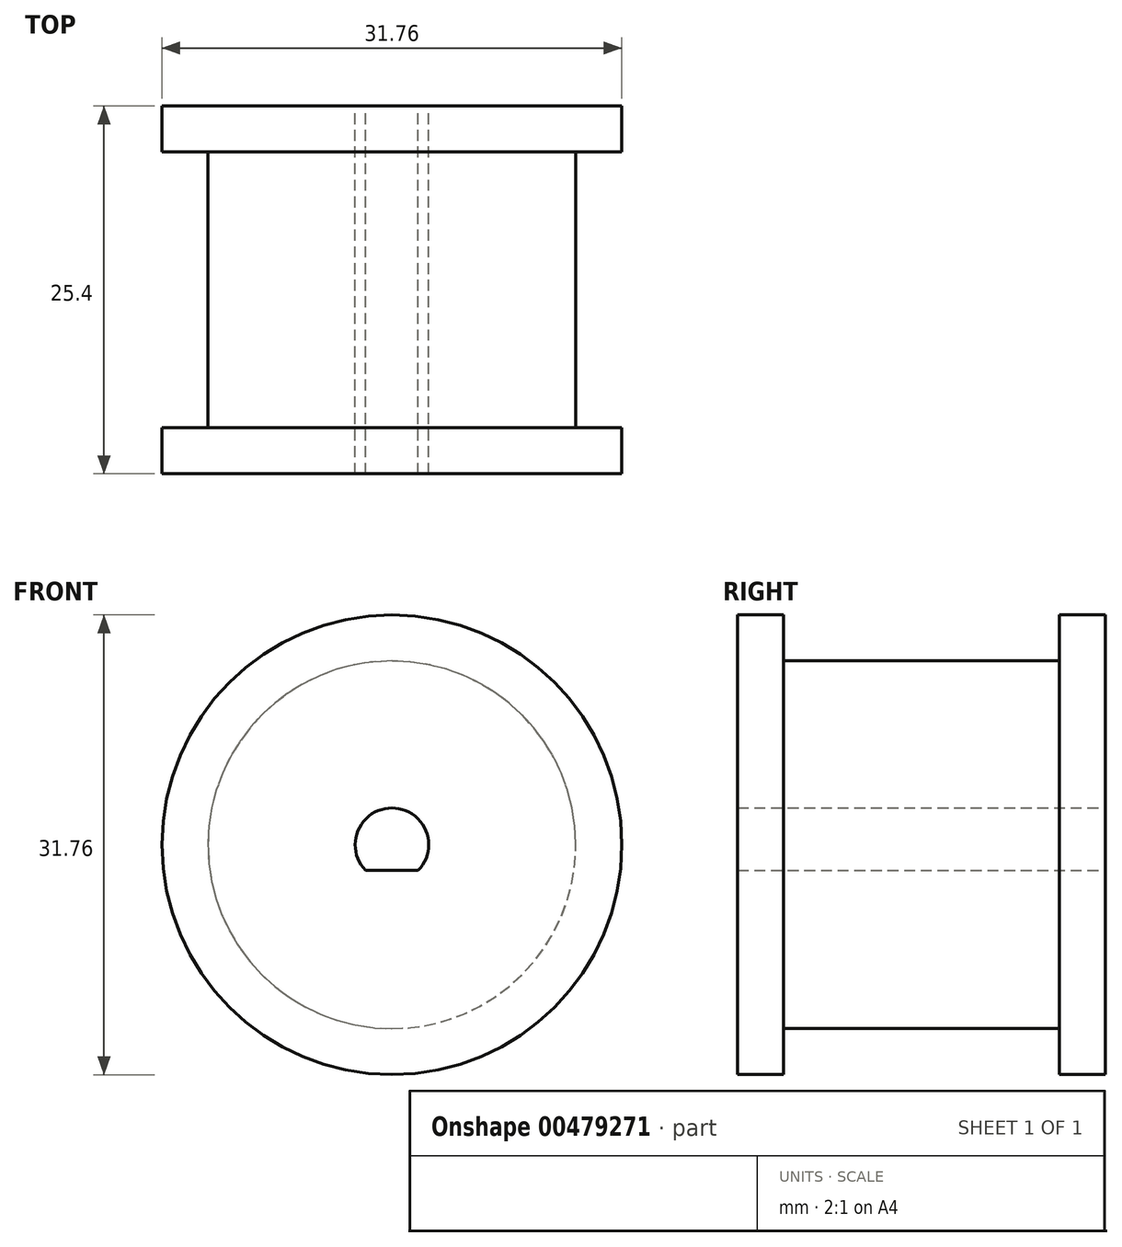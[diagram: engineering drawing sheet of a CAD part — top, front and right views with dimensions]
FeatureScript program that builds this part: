
annotation { "Feature Type Name" : "Feature", "Feature Type Description" : "" }
export const myFeature = defineFeature(function(context is Context, id is Id, definition is map)
    precondition{}
    {
        {
            var Q0;
            Q0=qCreatedBy(makeId("Front.planeOp"),FACE);
            var sketch = newSketch(context, id + "F0", { "sketchPlane" : qUnion([Q0])});
            skCircle(sketch, "E0", {"center": v(0, 0) * mm, "radius": 2.54 * mm});
            skLineSegment(sketch, "E1", {"start": v(-1.81, -1.78) * mm, "end": v(1.81, -1.78) * mm});
            skCircle(sketch, "E2", {"center": v(0, 0) * mm, "radius": 12.7 * mm});
            skSolve(sketch);
        }
        {
            var Q0;
            Q0 = qSketchRegion(id + "F0", true);
            var Q1;
            {var subQ0=sQuery(id+"F0.wireOp",EDGE,"E1");Q1=makeQuery(id+"F0.imprint","IMPRINT",FACE,{"disambiguationData":[TD([[makeQuery(id+"F0.imprint","IMPRINT",EDGE,{"derivedFrom":subQ0}),-1.0]])]});}
            extrude(context, id + "F1", {"entities" : qUnion([Q0, Q1]), "depth" : 25.4 * mm});
        }
        {
            var Q0;
            Q0=makeQuery(id+"F1.opExtrude","CAP_FACE",FACE,{"disambiguationData":[OSD([sQuery(id+"F0.wireOp",EDGE,"E0"),sQuery(id+"F0.wireOp",EDGE,"E2")])],"isStart":false});
            var sketch = newSketch(context, id + "F2", { "sketchPlane" : qUnion([Q0])});
            skCircle(sketch, "E3", {"center": v(0, 0) * mm, "radius": 15.88 * mm});
            skSolve(sketch);
        }
        {
            var Q0;
            Q0=makeQuery(id+"F2.imprint","IMPRINT",FACE,{"disambiguationData":[TD([[makeQuery(id+"F2.imprint","IMPRINT",EDGE,{"derivedFrom":sQuery(id+"F2.wireOp",EDGE,"E3")}),1.0]])]});
            var Q1;
            Q1=makeQuery(id+"F2.imprint","IMPRINT",FACE,{"disambiguationData":[TD([[makeQuery(id+"F2.imprint","IMPRINT",EDGE,{"derivedFrom":makeQuery(id+"F1.opExtrude","CAP_EDGE",EDGE,{"disambiguationData":[OSD([sQuery(id+"F0.wireOp",EDGE,"E0")])],"isStart":false})}),-1.0]])]});
            extrude(context, id + "F3", {"entities" : qUnion([Q0, Q1]), "operationType" : NewBodyOperationType.ADD, "oppositeDirection" : true, "depth" : 3.17 * mm});
        }
        {
            var Q0;
            Q0=makeQuery(id+"F1.opExtrude","CAP_FACE",FACE,{"disambiguationData":[OSD([sQuery(id+"F0.wireOp",EDGE,"E0"),sQuery(id+"F0.wireOp",EDGE,"E1"),sQuery(id+"F0.wireOp",EDGE,"E2")])],"isStart":true});
            var Q1;
            {var subQ0=sQuery(id+"F0.wireOp",EDGE,"E1");var subQ1=sQuery(id+"F0.wireOp",EDGE,"E0");Q1=makeQuery(id+"F3.boolean.opBoolean","MERGE",FACE,{"derivedFrom":[makeQuery(id+"F1.opExtrude","CAP_FACE",FACE,{"disambiguationData":[OSD([subQ1,subQ0,sQuery(id+"F0.wireOp",EDGE,"E2")])],"isStart":false}),makeQuery(id+"F3.opExtrude","CAP_FACE",FACE,{"disambiguationData":[OSD([subQ1,subQ0,sQuery(id+"F2.wireOp",EDGE,"E3")])],"isStart":true})]});}
            cPlane(context, id + "F4", {"entities" : qUnion([Q0, Q1]), "cplaneType" : CPlaneType.MID_PLANE, "offset" : 25.4 * mm, "width" : 152.4 * mm, "height" : 152.4 * mm});
        }
        {
            var Q0;
            Q0=makeQuery(id+"F1.opExtrude","SWEPT_BODY",BODY,{"disambiguationData":[OSD([sQuery(id+"F0.wireOp",EDGE,"E0"),sQuery(id+"F0.wireOp",EDGE,"E1"),sQuery(id+"F0.wireOp",EDGE,"E2")])]});
            var Q1;
            Q1=qCreatedBy(id+"F4.planeOp",FACE);
            mirror(context, id + "F5", {"operationType" : NewBodyOperationType.ADD, "entities" : qUnion([Q0]), "mirrorPlane" : qUnion([Q1])});
        }
    });
